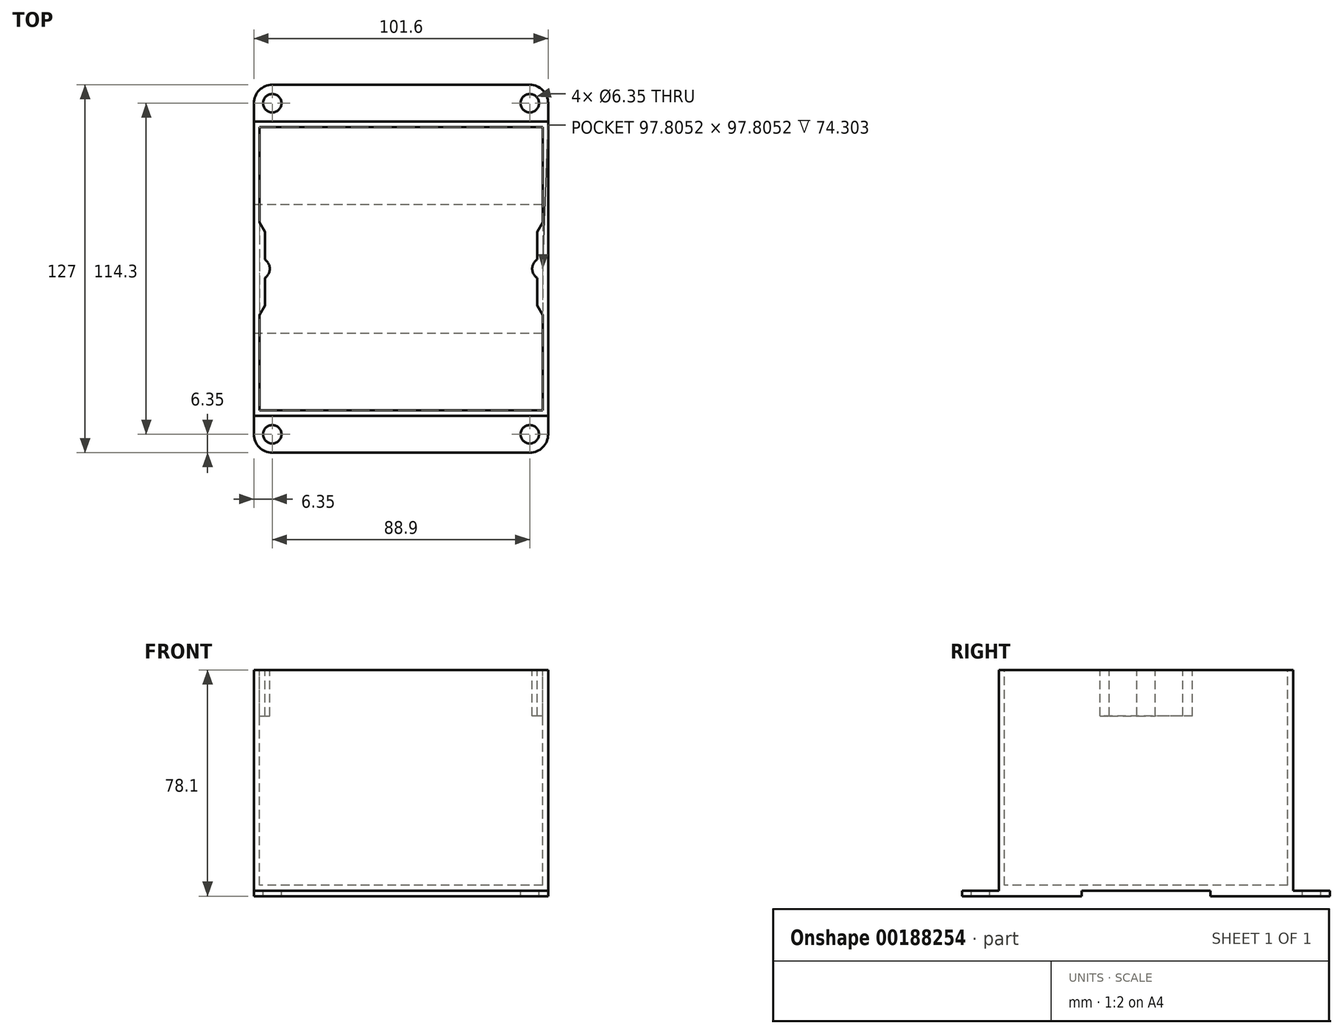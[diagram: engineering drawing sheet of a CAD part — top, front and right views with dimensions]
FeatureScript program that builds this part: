
annotation { "Feature Type Name" : "Feature", "Feature Type Description" : "" }
export const myFeature = defineFeature(function(context is Context, id is Id, definition is map)
    precondition{}
    {
        {
            var Q0;
            Q0=qCreatedBy(makeId("Top.planeOp"),FACE);
            var sketch = newSketch(context, id + "F0", { "sketchPlane" : qUnion([Q0])});
            skLineSegment(sketch, "E0.bottom", {"start": v(-50.8, 50.8) * mm, "end": v(50.8, 50.8) * mm});
            skLineSegment(sketch, "E0.top", {"start": v(-50.8, -50.8) * mm, "end": v(50.8, -50.8) * mm});
            skLineSegment(sketch, "E0.left", {"start": v(-50.8, 50.8) * mm, "end": v(-50.8, -50.8) * mm});
            skLineSegment(sketch, "E0.right", {"start": v(50.8, 50.8) * mm, "end": v(50.8, -50.8) * mm});
            skPoint(sketch, "E0.middle", {"position": v(0, 0) * mm});
            skSolve(sketch);
        }
        {
            var Q0;
            Q0 = qSketchRegion(id + "F0", true);
            extrude(context, id + "F1", {"entities" : qUnion([Q0]), "depth" : 76.2 * mm});
        }
        {
            var Q0;
            Q0=makeQuery(id+"F1.opExtrude","CAP_FACE",FACE,{"disambiguationData":[OSD([sQuery(id+"F0.wireOp",EDGE,"E0.bottom"),sQuery(id+"F0.wireOp",EDGE,"E0.top"),sQuery(id+"F0.wireOp",EDGE,"E0.left"),sQuery(id+"F0.wireOp",EDGE,"E0.right")])],"isStart":false});
            var sketch = newSketch(context, id + "F2", { "sketchPlane" : qUnion([Q0])});
            skLineSegment(sketch, "E1.bottom", {"start": v(48.9, 48.9) * mm, "end": v(-48.9, 48.9) * mm});
            skLineSegment(sketch, "E1.top", {"start": v(48.9, -48.9) * mm, "end": v(-48.9, -48.9) * mm});
            skLineSegment(sketch, "E1.left", {"start": v(48.9, 48.9) * mm, "end": v(48.9, -48.9) * mm});
            skLineSegment(sketch, "E1.right", {"start": v(-48.9, 48.9) * mm, "end": v(-48.9, -48.9) * mm});
            skPoint(sketch, "E1.middle", {"position": v(0, 0) * mm});
            skSolve(sketch);
        }
        {
            var Q0;
            Q0 = qSketchRegion(id + "F2", true);
            extrude(context, id + "F3", {"entities" : qUnion([Q0]), "operationType" : NewBodyOperationType.REMOVE, "oppositeDirection" : true, "depth" : 74.3 * mm});
        }
        {
            var Q0;
            Q0=makeQuery(id+"F1.opExtrude","CAP_FACE",FACE,{"disambiguationData":[OSD([sQuery(id+"F0.wireOp",EDGE,"E0.bottom"),sQuery(id+"F0.wireOp",EDGE,"E0.top"),sQuery(id+"F0.wireOp",EDGE,"E0.left"),sQuery(id+"F0.wireOp",EDGE,"E0.right")])],"isStart":false});
            var sketch = newSketch(context, id + "F4", { "sketchPlane" : qUnion([Q0])});
            skLineSegment(sketch, "E2", {"start": v(-48.9, 15.99) * mm, "end": v(-47, 12.7) * mm});
            skLineSegment(sketch, "E3", {"start": v(-47, 12.7) * mm, "end": v(-47, 3.17) * mm});
            skLineSegment(sketch, "E4", {"start": v(-48.9, -15.99) * mm, "end": v(-47, -12.7) * mm});
            skLineSegment(sketch, "E5", {"start": v(-47, -12.7) * mm, "end": v(-47, -3.18) * mm});
            skLineSegment(sketch, "E6", {"start": v(48.9, 15.99) * mm, "end": v(47, 12.7) * mm});
            skLineSegment(sketch, "E7", {"start": v(47, 12.7) * mm, "end": v(47, 3.18) * mm});
            skLineSegment(sketch, "E8", {"start": v(48.9, -15.99) * mm, "end": v(47, -12.7) * mm});
            skLineSegment(sketch, "E9", {"start": v(47, -12.7) * mm, "end": v(47, -3.17) * mm});
            skArc(sketch, "E10", {"start": v(-47, -3.18) * mm, "mid": v(-45.3, 0) * mm, "end": v(-47, 3.17) * mm});
            skArc(sketch, "E11", {"start": v(47, 3.18) * mm, "mid": v(45.3, 0) * mm, "end": v(47, -3.17) * mm});
            skLineSegment(sketch, "E12", {"start": v(-48.9, -15.99) * mm, "end": v(-48.9, 15.99) * mm});
            skLineSegment(sketch, "E13", {"start": v(48.9, -15.99) * mm, "end": v(48.9, 15.99) * mm});
            skSolve(sketch);
        }
        {
            var Q0;
            Q0 = qSketchRegion(id + "F4", true);
            extrude(context, id + "F5", {"entities" : qUnion([Q0]), "operationType" : NewBodyOperationType.ADD, "oppositeDirection" : true, "depth" : 15.88 * mm});
        }
        {
            var Q0;
            Q0=makeQuery(id+"F1.opExtrude","CAP_FACE",FACE,{"disambiguationData":[OSD([sQuery(id+"F0.wireOp",EDGE,"E0.bottom"),sQuery(id+"F0.wireOp",EDGE,"E0.top"),sQuery(id+"F0.wireOp",EDGE,"E0.left"),sQuery(id+"F0.wireOp",EDGE,"E0.right")])],"isStart":true});
            var sketch = newSketch(context, id + "F6", { "sketchPlane" : qUnion([Q0])});
            skLineSegment(sketch, "E14", {"start": v(-50.8, 22.23) * mm, "end": v(50.8, 22.23) * mm});
            skLineSegment(sketch, "E15", {"start": v(50.8, 22.23) * mm, "end": v(50.8, 57.15) * mm});
            skLineSegment(sketch, "E16", {"start": v(44.45, 63.5) * mm, "end": v(-44.45, 63.5) * mm});
            skLineSegment(sketch, "E17", {"start": v(-50.8, 57.15) * mm, "end": v(-50.8, 22.23) * mm});
            skPoint(sketch, "E18.visualSharp", {"position": v(-50.8, 63.5) * mm});
            skArc(sketch, "E18.filletArc", {"start": v(-44.45, 63.5) * mm, "mid": v(-48.94, 61.64) * mm, "end": v(-50.8, 57.15) * mm});
            skPoint(sketch, "E19.visualSharp", {"position": v(50.8, 63.5) * mm});
            skArc(sketch, "E19.filletArc", {"start": v(50.8, 57.15) * mm, "mid": v(48.94, 61.64) * mm, "end": v(44.45, 63.5) * mm});
            skCircle(sketch, "E20", {"center": v(-44.45, 57.15) * mm, "radius": 3.18 * mm});
            skCircle(sketch, "E21", {"center": v(44.45, 57.15) * mm, "radius": 3.18 * mm});
            skLineSegment(sketch, "E22", {"start": v(-61.36, 0) * mm, "end": v(78.94, 0) * mm});
            skLineSegment(sketch, "E23.MirrorCS", {"start": v(-50.8, -22.23) * mm, "end": v(50.8, -22.23) * mm});
            skLineSegment(sketch, "E24.MirrorCS", {"start": v(-50.8, -57.15) * mm, "end": v(-50.8, -22.23) * mm});
            skArc(sketch, "E25.MirrorCS", {"start": v(-44.45, -63.5) * mm, "mid": v(-48.94, -61.64) * mm, "end": v(-50.8, -57.15) * mm});
            skCircle(sketch, "E26.MirrorC", {"center": v(-44.45, -57.15) * mm, "radius": 3.18 * mm});
            skLineSegment(sketch, "E27.MirrorCS", {"start": v(44.45, -63.5) * mm, "end": v(-44.45, -63.5) * mm});
            skCircle(sketch, "E28.MirrorC", {"center": v(44.45, -57.15) * mm, "radius": 3.18 * mm});
            skLineSegment(sketch, "E29.MirrorCS", {"start": v(50.8, -22.23) * mm, "end": v(50.8, -57.15) * mm});
            skArc(sketch, "E30.MirrorCS", {"start": v(50.8, -57.15) * mm, "mid": v(48.94, -61.64) * mm, "end": v(44.45, -63.5) * mm});
            skSolve(sketch);
        }
        {
            var Q0;
            Q0 = qSketchRegion(id + "F6", true);
            extrude(context, id + "F7", {"entities" : qUnion([Q0]), "operationType" : NewBodyOperationType.ADD, "depth" : 1.9 * mm});
        }
    });
